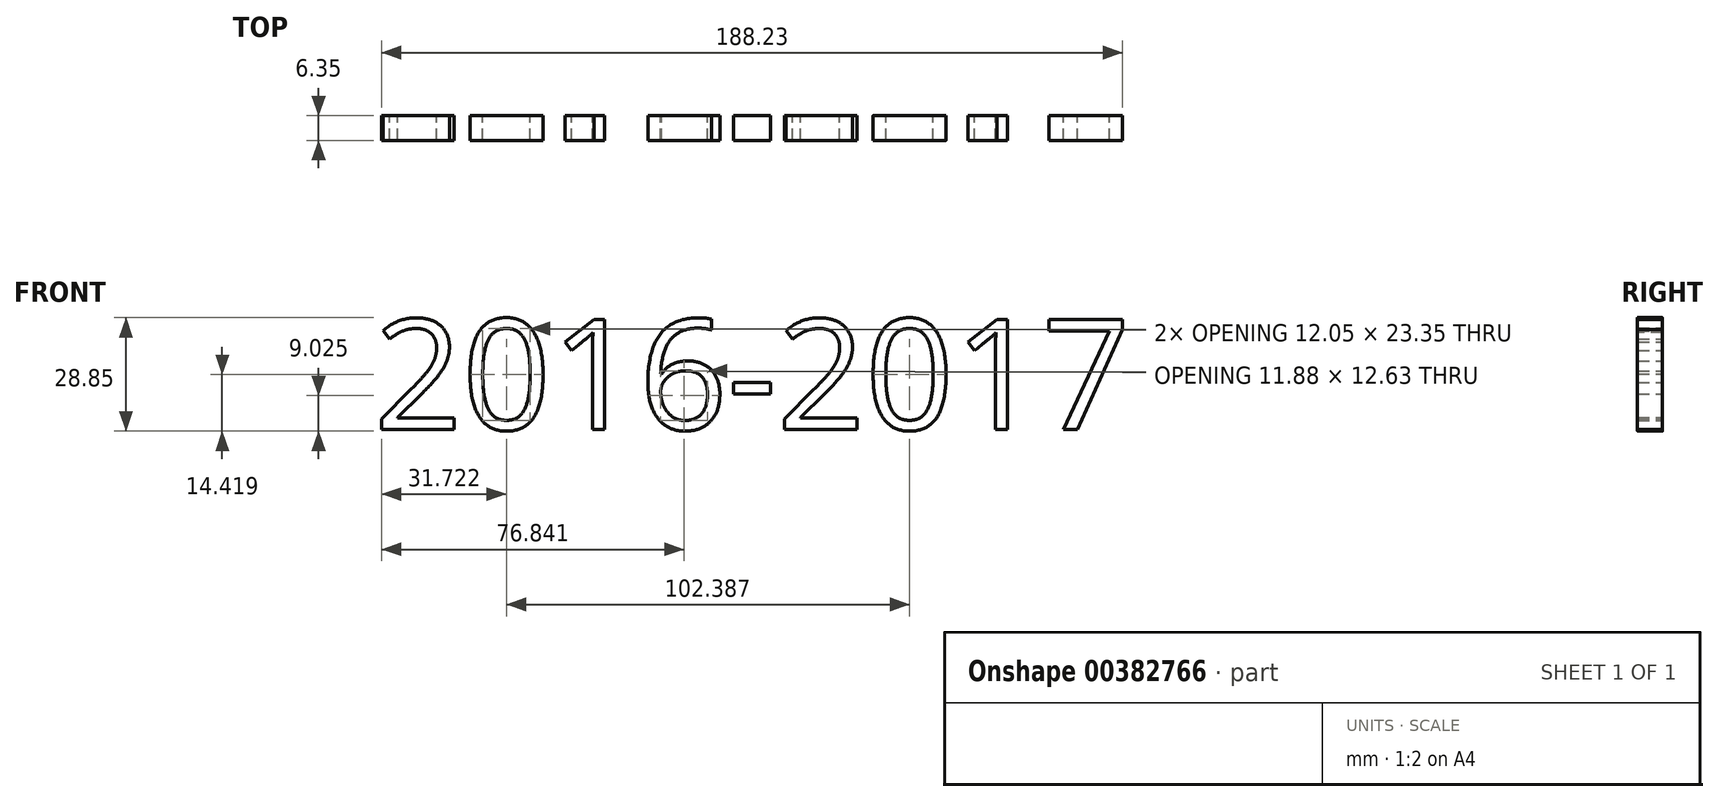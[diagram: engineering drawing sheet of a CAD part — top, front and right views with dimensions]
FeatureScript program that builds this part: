
annotation { "Feature Type Name" : "Feature", "Feature Type Description" : "" }
export const myFeature = defineFeature(function(context is Context, id is Id, definition is map)
    precondition{}
    {
        {
            var Q0;
            Q0=qCreatedBy(makeId("Front.planeOp"),FACE);
            var sketch = newSketch(context, id + "F0", { "sketchPlane" : qUnion([Q0])});
            skText(sketch, "E0", { "text": "2016-2017", "fontName": "OpenSans-Regular.ttf"});
            const initialGuessF0  = {"E0": [-0.09554, -0.01902, 1, 0, 0.02826]};
            skSetInitialGuess(sketch, initialGuessF0);
            skSolve(sketch);
        }
        {
            var Q0;
            Q0 = qSketchRegion(id + "F0", true);
            extrude(context, id + "F1", {"entities" : qUnion([Q0]), "depth" : 6.35 * mm});
        }
    });
